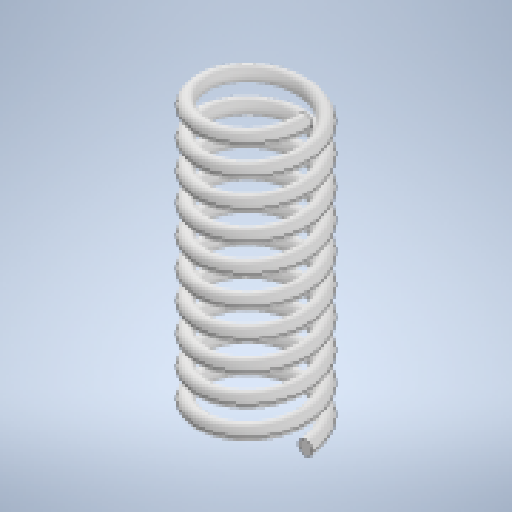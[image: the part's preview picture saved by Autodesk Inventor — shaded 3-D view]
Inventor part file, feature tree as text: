
AUTODESK INVENTOR PART (.ipt)
format: ipt  version: 2023 (Build 270158000, 158)  size: 386,048 bytes
history: native  units: mm
features: sketch x3, revolve x2, helix x1
ambient origin geometry x8: Origin, YZ Plane, XZ Plane, XY Plane, X Axis, Y Axis, Z Axis, Center Point
bodies: Solid1 (feature_tree)
feature tree (6):
  helix  "Coil1"  [1 undecoded]
  revolve  "Revolution1"  [1 undecoded]
  revolve  "Revolution2"  [1 undecoded]
  sketch  "Sketch1"  dims[d1=3.5mm]
  sketch  "Sketch2"  dims[d2=2.0mm d3=10.0mm d4=70.0mm d5=0.0mm d6=90.0deg d7=90.0deg d8=0.0mm d9=0.0mm d10=3.5mm]
  sketch  "Sketch3"  dims[d11=34.906585mm d12=3.5mm d13=34.906585mm]
note: 3 required parameter values undecoded (feature->parameter linkage not recoverable at this tier; creation-order binding heuristic only, values carry confidence <= 0.55)